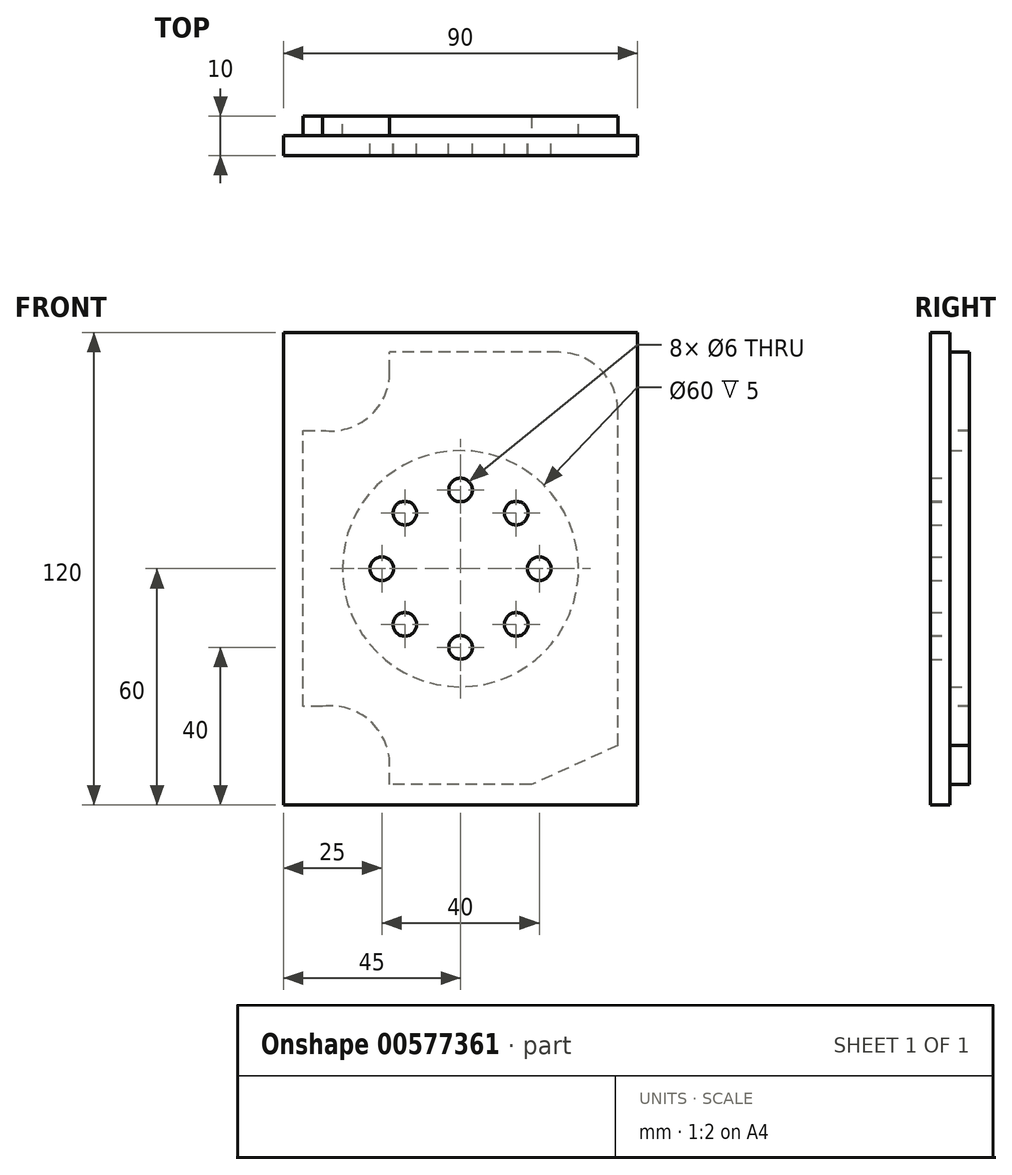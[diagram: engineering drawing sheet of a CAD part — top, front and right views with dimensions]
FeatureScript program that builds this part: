
annotation { "Feature Type Name" : "Feature", "Feature Type Description" : "" }
export const myFeature = defineFeature(function(context is Context, id is Id, definition is map)
    precondition{}
    {
        {
            var Q0;
            Q0=qCreatedBy(makeId("Front.planeOp"),FACE);
            var sketch = newSketch(context, id + "F0", { "sketchPlane" : qUnion([Q0])});
            skLineSegment(sketch, "E0", {"start": v(0, 0) * mm, "end": v(90, 0) * mm});
            skLineSegment(sketch, "E1", {"start": v(90, 0) * mm, "end": v(90, -120) * mm});
            skLineSegment(sketch, "E2", {"start": v(90, -120) * mm, "end": v(0, -120) * mm});
            skLineSegment(sketch, "E3", {"start": v(0, -120) * mm, "end": v(0, 0) * mm});
            skSolve(sketch);
        }
        {
            var Q0;
            Q0=makeQuery(id+"F0.imprint","IMPRINT",FACE,{"disambiguationData":[TD([[makeQuery(id+"F0.imprint","IMPRINT",EDGE,{"derivedFrom":sQuery(id+"F0.wireOp",EDGE,"E0")}),-1.0]])]});
            extrude(context, id + "F1", {"entities" : qUnion([Q0]), "depth" : 5 * mm, "offsetDistance" : 25 * mm});
        }
        {
            var Q0;
            Q0=makeQuery(id+"F1.opExtrude","CAP_FACE",FACE,{"disambiguationData":[OSD([sQuery(id+"F0.wireOp",EDGE,"E0"),sQuery(id+"F0.wireOp",EDGE,"E1"),sQuery(id+"F0.wireOp",EDGE,"E2"),sQuery(id+"F0.wireOp",EDGE,"E3")])],"isStart":true});
            var sketch = newSketch(context, id + "F2", { "sketchPlane" : qUnion([Q0])});
            skLineSegment(sketch, "E4", {"start": v(-63, -114.87) * mm, "end": v(-27, -114.87) * mm});
            skLineSegment(sketch, "E5", {"start": v(-27, -114.87) * mm, "end": v(-27, -109.87) * mm});
            skArc(sketch, "E6", {"start": v(-10, -95) * mm, "mid": v(-21.87, -98.57) * mm, "end": v(-27, -109.87) * mm});
            skLineSegment(sketch, "E7", {"start": v(-10, -95) * mm, "end": v(-5, -95) * mm});
            skLineSegment(sketch, "E8", {"start": v(-5, -95) * mm, "end": v(-5, -24.87) * mm});
            skLineSegment(sketch, "E9", {"start": v(-5, -24.87) * mm, "end": v(-10, -24.87) * mm});
            skLineSegment(sketch, "E10", {"start": v(-27, -10) * mm, "end": v(-27, -5) * mm});
            skLineSegment(sketch, "E11", {"start": v(-85, -104.87) * mm, "end": v(-63, -114.87) * mm});
            skArc(sketch, "E12", {"start": v(-70, -5) * mm, "mid": v(-80.6, -9.4) * mm, "end": v(-85, -20) * mm});
            skLineSegment(sketch, "E13", {"start": v(-85, -104.87) * mm, "end": v(-85, -20) * mm});
            skLineSegment(sketch, "E14", {"start": v(-70, -5) * mm, "end": v(-27, -5) * mm});
            skArc(sketch, "E15", {"start": v(-27, -10) * mm, "mid": v(-21.87, -21.3) * mm, "end": v(-10, -24.87) * mm});
            skSolve(sketch);
        }
        {
            var Q0;
            Q0=makeQuery(id+"F2.imprint","IMPRINT",FACE,{"disambiguationData":[TD([[makeQuery(id+"F2.imprint","IMPRINT",EDGE,{"derivedFrom":sQuery(id+"F2.wireOp",EDGE,"E4")}),1.0]])]});
            extrude(context, id + "F3", {"entities" : qUnion([Q0]), "operationType" : NewBodyOperationType.ADD, "depth" : 5 * mm, "offsetDistance" : 25 * mm});
        }
        {
            var Q0;
            Q0=makeQuery(id+"F3.opExtrude","CAP_FACE",FACE,{"disambiguationData":[OSD([sQuery(id+"F2.wireOp",EDGE,"E4"),sQuery(id+"F2.wireOp",EDGE,"E5"),sQuery(id+"F2.wireOp",EDGE,"E6"),sQuery(id+"F2.wireOp",EDGE,"E7"),sQuery(id+"F2.wireOp",EDGE,"E8"),sQuery(id+"F2.wireOp",EDGE,"E9"),sQuery(id+"F2.wireOp",EDGE,"E10"),sQuery(id+"F2.wireOp",EDGE,"E11"),sQuery(id+"F2.wireOp",EDGE,"E12"),sQuery(id+"F2.wireOp",EDGE,"E13"),sQuery(id+"F2.wireOp",EDGE,"E14"),sQuery(id+"F2.wireOp",EDGE,"E15")])],"isStart":false});
            var sketch = newSketch(context, id + "F4", { "sketchPlane" : qUnion([Q0])});
            skCircle(sketch, "E16", {"center": v(-45, -60) * mm, "radius": 30 * mm});
            skLineSegment(sketch, "E17", {"start": v(-45, -60) * mm, "end": v(-45, -90) * mm, "construction": true});
            skLineSegment(sketch, "E18", {"start": v(-45, -60) * mm, "end": v(-45, -30) * mm, "construction": true});
            skLineSegment(sketch, "E19", {"start": v(-45, -60) * mm, "end": v(-75, -60) * mm, "construction": true});
            skLineSegment(sketch, "E20", {"start": v(-45, -60) * mm, "end": v(-15, -60) * mm, "construction": true});
            skCircle(sketch, "E21", {"center": v(-25, -60) * mm, "radius": 3 * mm});
            skCircle(sketch, "E22", {"center": v(-45, -40) * mm, "radius": 3 * mm});
            skCircle(sketch, "E23", {"center": v(-30.86, -45.86) * mm, "radius": 3 * mm});
            skCircle(sketch, "E24", {"center": v(-45, -80) * mm, "radius": 3 * mm});
            skCircle(sketch, "E25", {"center": v(-65, -60) * mm, "radius": 3 * mm});
            skCircle(sketch, "E26", {"center": v(-59.14, -45.86) * mm, "radius": 3 * mm});
            skCircle(sketch, "E27", {"center": v(-30.86, -74.14) * mm, "radius": 3 * mm});
            skCircle(sketch, "E28", {"center": v(-59.14, -74.14) * mm, "radius": 3 * mm});
            skCircle(sketch, "E29", {"center": v(-45, -60) * mm, "radius": 20 * mm, "construction": true});
            skSolve(sketch);
        }
        {
            var Q0;
            Q0=makeQuery(id+"F4.imprint","IMPRINT",FACE,{"disambiguationData":[TD([[makeQuery(id+"F4.imprint","IMPRINT",EDGE,{"derivedFrom":sQuery(id+"F4.wireOp",EDGE,"E16")}),1.0]])]});
            extrude(context, id + "F5", {"entities" : qUnion([Q0]), "operationType" : NewBodyOperationType.REMOVE, "oppositeDirection" : true, "depth" : 5 * mm, "offsetDistance" : 25 * mm});
        }
        {
            var Q0;
            {var subQ3=sQuery(id+"F4.wireOp",EDGE,"E21");Q0=makeQuery(id+"F5.boolean.opBoolean","SPLIT",FACE,{"disambiguationData":[TD([makeQuery(id+"F5.opExtrude","SWEPT_FACE",FACE,{"disambiguationData":[OSD([subQ3])]})])],"derivedFrom":makeQuery(id+"F3.opExtrude","CAP_FACE",FACE,{"disambiguationData":[OSD([sQuery(id+"F2.wireOp",EDGE,"E4"),sQuery(id+"F2.wireOp",EDGE,"E5"),sQuery(id+"F2.wireOp",EDGE,"E6"),sQuery(id+"F2.wireOp",EDGE,"E7"),sQuery(id+"F2.wireOp",EDGE,"E8"),sQuery(id+"F2.wireOp",EDGE,"E9"),sQuery(id+"F2.wireOp",EDGE,"E10"),sQuery(id+"F2.wireOp",EDGE,"E11"),sQuery(id+"F2.wireOp",EDGE,"E12"),sQuery(id+"F2.wireOp",EDGE,"E13"),sQuery(id+"F2.wireOp",EDGE,"E14"),sQuery(id+"F2.wireOp",EDGE,"E15")])],"isStart":false})});}
            extrude(context, id + "F6", {"entities" : qUnion([Q0]), "operationType" : NewBodyOperationType.REMOVE, "oppositeDirection" : true, "depth" : 5 * mm, "offsetDistance" : 25 * mm});
        }
        {
            var Q0;
            Q0=makeQuery(id+"F4.imprint","IMPRINT",FACE,{"disambiguationData":[TD([[makeQuery(id+"F4.imprint","IMPRINT",EDGE,{"derivedFrom":sQuery(id+"F4.wireOp",EDGE,"E24")}),1.0]])]});
            var Q1;
            Q1=makeQuery(id+"F4.imprint","IMPRINT",FACE,{"disambiguationData":[TD([[makeQuery(id+"F4.imprint","IMPRINT",EDGE,{"derivedFrom":sQuery(id+"F4.wireOp",EDGE,"E27")}),1.0]])]});
            var Q2;
            Q2=makeQuery(id+"F4.imprint","IMPRINT",FACE,{"disambiguationData":[TD([[makeQuery(id+"F4.imprint","IMPRINT",EDGE,{"derivedFrom":sQuery(id+"F4.wireOp",EDGE,"E26")}),1.0]])]});
            var Q3;
            Q3=makeQuery(id+"F4.imprint","IMPRINT",FACE,{"disambiguationData":[TD([[makeQuery(id+"F4.imprint","IMPRINT",EDGE,{"derivedFrom":sQuery(id+"F4.wireOp",EDGE,"E25")}),1.0]])]});
            var Q4;
            Q4=makeQuery(id+"F4.imprint","IMPRINT",FACE,{"disambiguationData":[TD([[makeQuery(id+"F4.imprint","IMPRINT",EDGE,{"derivedFrom":sQuery(id+"F4.wireOp",EDGE,"E28")}),1.0]])]});
            var Q5;
            Q5=makeQuery(id+"F4.imprint","IMPRINT",FACE,{"disambiguationData":[TD([[makeQuery(id+"F4.imprint","IMPRINT",EDGE,{"derivedFrom":sQuery(id+"F4.wireOp",EDGE,"E23")}),1.0]])]});
            var Q6;
            Q6=makeQuery(id+"F4.imprint","IMPRINT",FACE,{"disambiguationData":[TD([[makeQuery(id+"F4.imprint","IMPRINT",EDGE,{"derivedFrom":sQuery(id+"F4.wireOp",EDGE,"E22")}),1.0]])]});
            var Q7;
            Q7=makeQuery(id+"F4.imprint","IMPRINT",FACE,{"disambiguationData":[TD([[makeQuery(id+"F4.imprint","IMPRINT",EDGE,{"derivedFrom":sQuery(id+"F4.wireOp",EDGE,"E21")}),1.0]])]});
            extrude(context, id + "F7", {"entities" : qUnion([Q0, Q1, Q2, Q3, Q4, Q5, Q6, Q7]), "operationType" : NewBodyOperationType.REMOVE, "oppositeDirection" : true, "depth" : 10 * mm, "offsetDistance" : 25 * mm});
        }
    });
